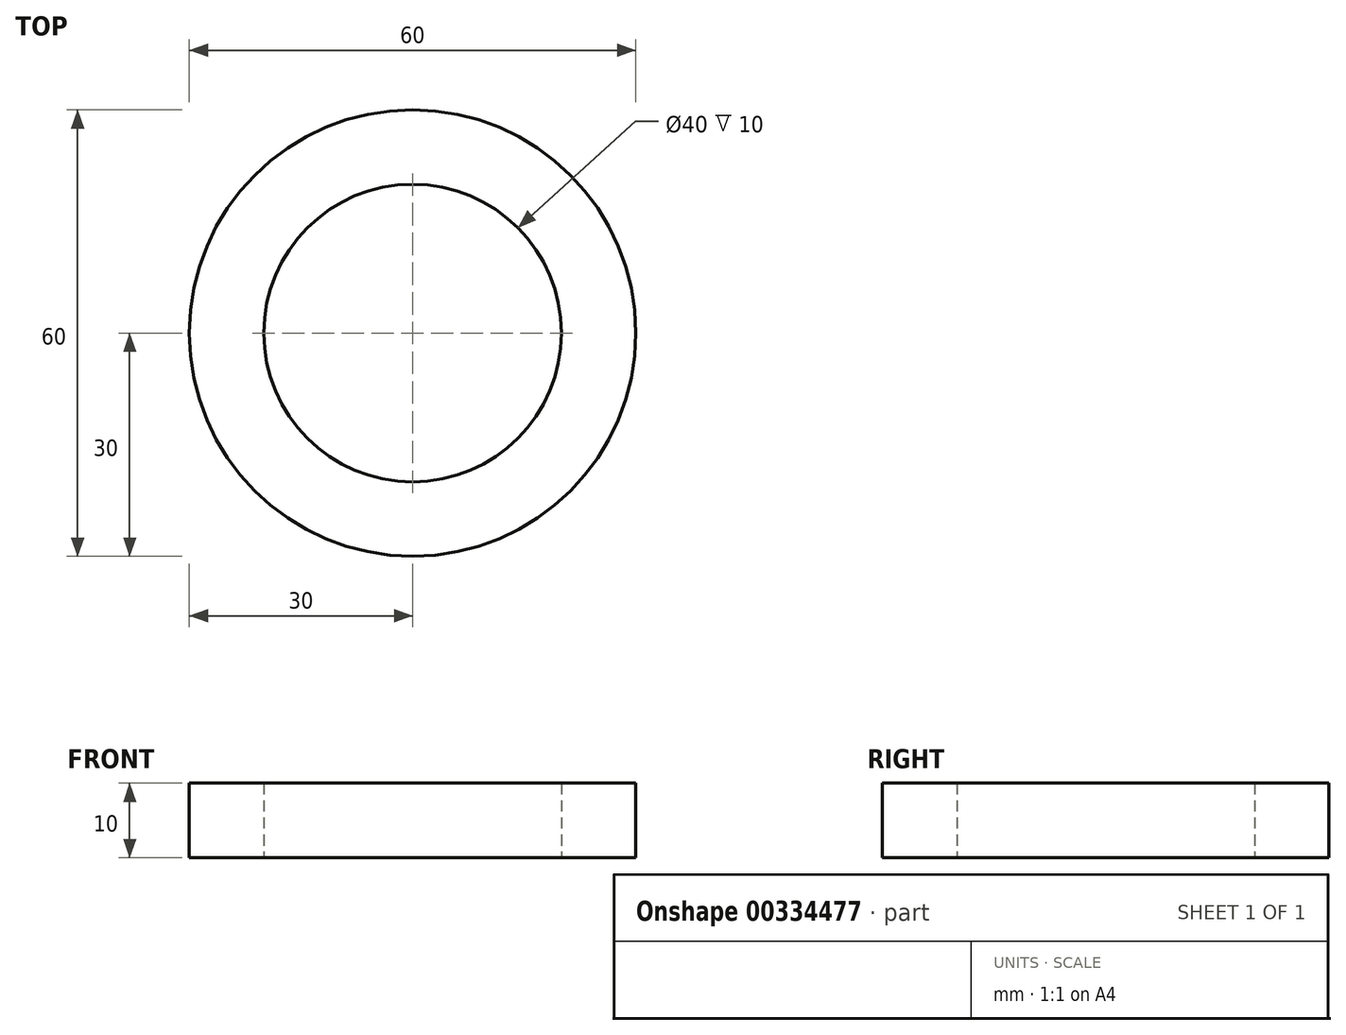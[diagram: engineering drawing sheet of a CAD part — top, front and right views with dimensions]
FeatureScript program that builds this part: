
annotation { "Feature Type Name" : "Feature", "Feature Type Description" : "" }
export const myFeature = defineFeature(function(context is Context, id is Id, definition is map)
    precondition{}
    {
        {
            var Q0;
            Q0=qCreatedBy(makeId("Top.planeOp"),FACE);
            var sketch = newSketch(context, id + "F0", { "sketchPlane" : qUnion([Q0])});
            skCircle(sketch, "E0", {"center": v(0, 0) * mm, "radius": 20 * mm});
            skCircle(sketch, "E1", {"center": v(0, 0) * mm, "radius": 30 * mm});
            skSolve(sketch);
        }
        {
            var Q0;
            Q0=makeQuery(id+"F0.imprint","IMPRINT",FACE,{"disambiguationData":[TD([[makeQuery(id+"F0.imprint","IMPRINT",EDGE,{"derivedFrom":sQuery(id+"F0.wireOp",EDGE,"E0")}),-1.0]])]});
            extrude(context, id + "F1", {"entities" : qUnion([Q0]), "depth" : 10 * mm});
        }
    });
